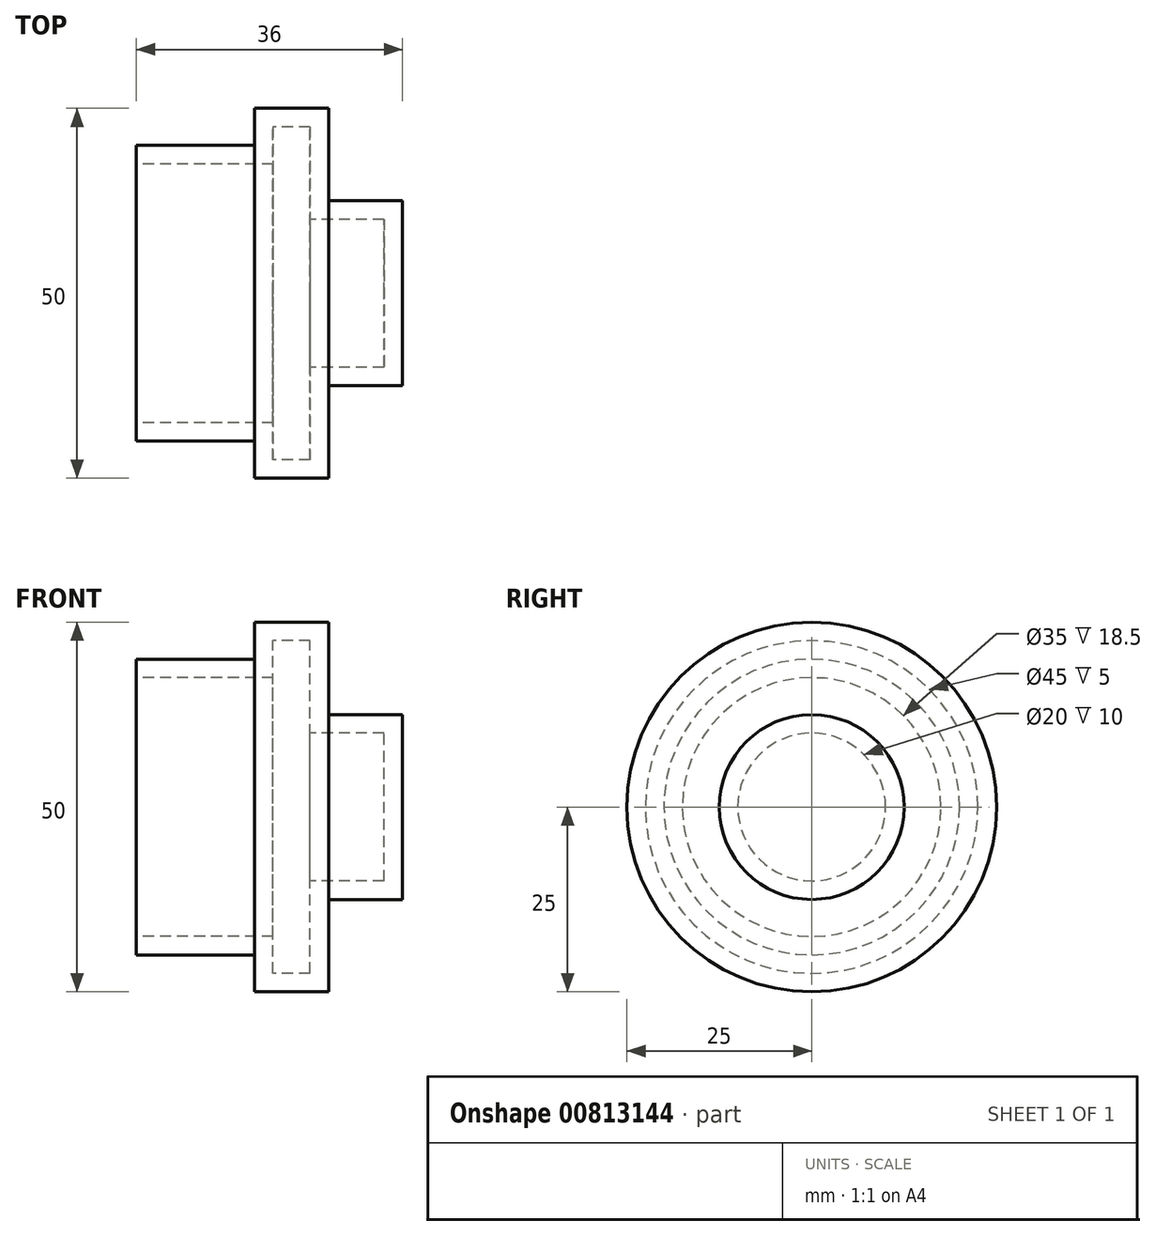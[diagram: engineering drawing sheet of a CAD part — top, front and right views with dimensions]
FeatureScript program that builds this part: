
annotation { "Feature Type Name" : "Feature", "Feature Type Description" : "" }
export const myFeature = defineFeature(function(context is Context, id is Id, definition is map)
    precondition{}
    {
        {
            var Q0;
            Q0=qCreatedBy(makeId("Right.planeOp"),FACE);
            var sketch = newSketch(context, id + "F0", { "sketchPlane" : qUnion([Q0])});
            skCircle(sketch, "E0", {"center": v(0, 0) * mm, "radius": 20 * mm});
            skSolve(sketch);
        }
        {
            var Q0;
            Q0=makeQuery(id+"F0.imprint","IMPRINT",FACE,{"disambiguationData":[TD([[makeQuery(id+"F0.imprint","IMPRINT",EDGE,{"derivedFrom":sQuery(id+"F0.wireOp",EDGE,"E0")}),1.0]])]});
            extrude(context, id + "F1", {"entities" : qUnion([Q0]), "depth" : 16 * mm, "offsetDistance" : 25 * mm});
        }
        {
            var Q0;
            Q0=makeQuery(id+"F1.opExtrude","CAP_FACE",FACE,{"disambiguationData":[OSD([sQuery(id+"F0.wireOp",EDGE,"E0")])],"isStart":false});
            var sketch = newSketch(context, id + "F2", { "sketchPlane" : qUnion([Q0])});
            skCircle(sketch, "E1", {"center": v(0, 0) * mm, "radius": 25 * mm});
            skSolve(sketch);
        }
        {
            var Q0;
            Q0=makeQuery(id+"F2.imprint","IMPRINT",FACE,{"disambiguationData":[TD([[makeQuery(id+"F2.imprint","IMPRINT",EDGE,{"derivedFrom":sQuery(id+"F2.wireOp",EDGE,"E1")}),1.0]])]});
            var Q1;
            Q1=makeQuery(id+"F2.imprint","IMPRINT",FACE,{"disambiguationData":[TD([[makeQuery(id+"F2.imprint","IMPRINT",EDGE,{"derivedFrom":makeQuery(id+"F1.opExtrude","CAP_EDGE",EDGE,{"disambiguationData":[OSD([sQuery(id+"F0.wireOp",EDGE,"E0")])],"isStart":false})}),1.0]])]});
            extrude(context, id + "F3", {"entities" : qUnion([Q0, Q1]), "operationType" : NewBodyOperationType.ADD, "depth" : 10 * mm, "offsetDistance" : 25 * mm});
        }
        {
            var Q0;
            Q0=makeQuery(id+"F3.opExtrude","CAP_FACE",FACE,{"disambiguationData":[OSD([sQuery(id+"F2.wireOp",EDGE,"E1")])],"isStart":false});
            var sketch = newSketch(context, id + "F4", { "sketchPlane" : qUnion([Q0])});
            skCircle(sketch, "E2", {"center": v(0, 0) * mm, "radius": 12.5 * mm});
            skSolve(sketch);
        }
        {
            var Q0;
            Q0=makeQuery(id+"F4.imprint","IMPRINT",FACE,{"disambiguationData":[TD([[makeQuery(id+"F4.imprint","IMPRINT",EDGE,{"derivedFrom":sQuery(id+"F4.wireOp",EDGE,"E2")}),1.0]])]});
            extrude(context, id + "F5", {"entities" : qUnion([Q0]), "operationType" : NewBodyOperationType.ADD, "depth" : 10 * mm, "offsetDistance" : 25 * mm});
        }
        {
            var Q0;
            Q0=makeQuery(id+"F1.opExtrude","CAP_FACE",FACE,{"disambiguationData":[OSD([sQuery(id+"F0.wireOp",EDGE,"E0")])],"isStart":true});
            shell(context, id + "F6", {"entities" : qUnion([Q0]), "thickness" : 2.5 * mm});
        }
    });
